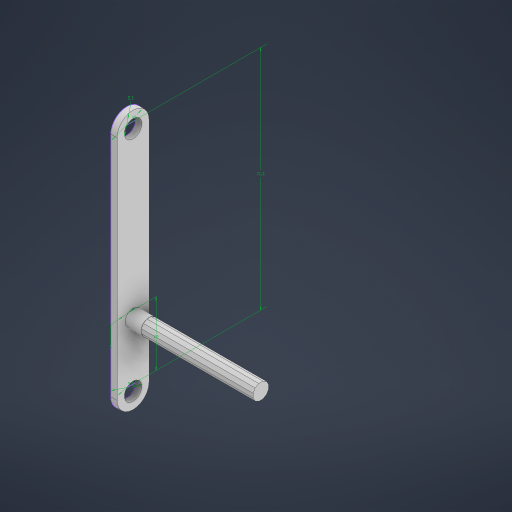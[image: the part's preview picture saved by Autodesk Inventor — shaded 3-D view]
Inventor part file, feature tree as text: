
AUTODESK INVENTOR PART (.ipt)
format: ipt  version: 2024 (Build 280153000, 153)  size: 229,888 bytes
history: native  units: mm
features: extrude x3, other x1, sketch x1
ambient origin geometry x8: Origin, YZ Plane, XZ Plane, XY Plane, X Axis, Y Axis, Z Axis, Center Point
bodies: Body1 (feature_tree)
feature tree (5):
  other  "솔리드1"
  sketch  "스케치1"
  extrude  "돌출1"  Depth=5.0mm
  extrude  "돌출2"  Depth=5.5mm
  extrude  "돌출3"  Depth=10.0mm
